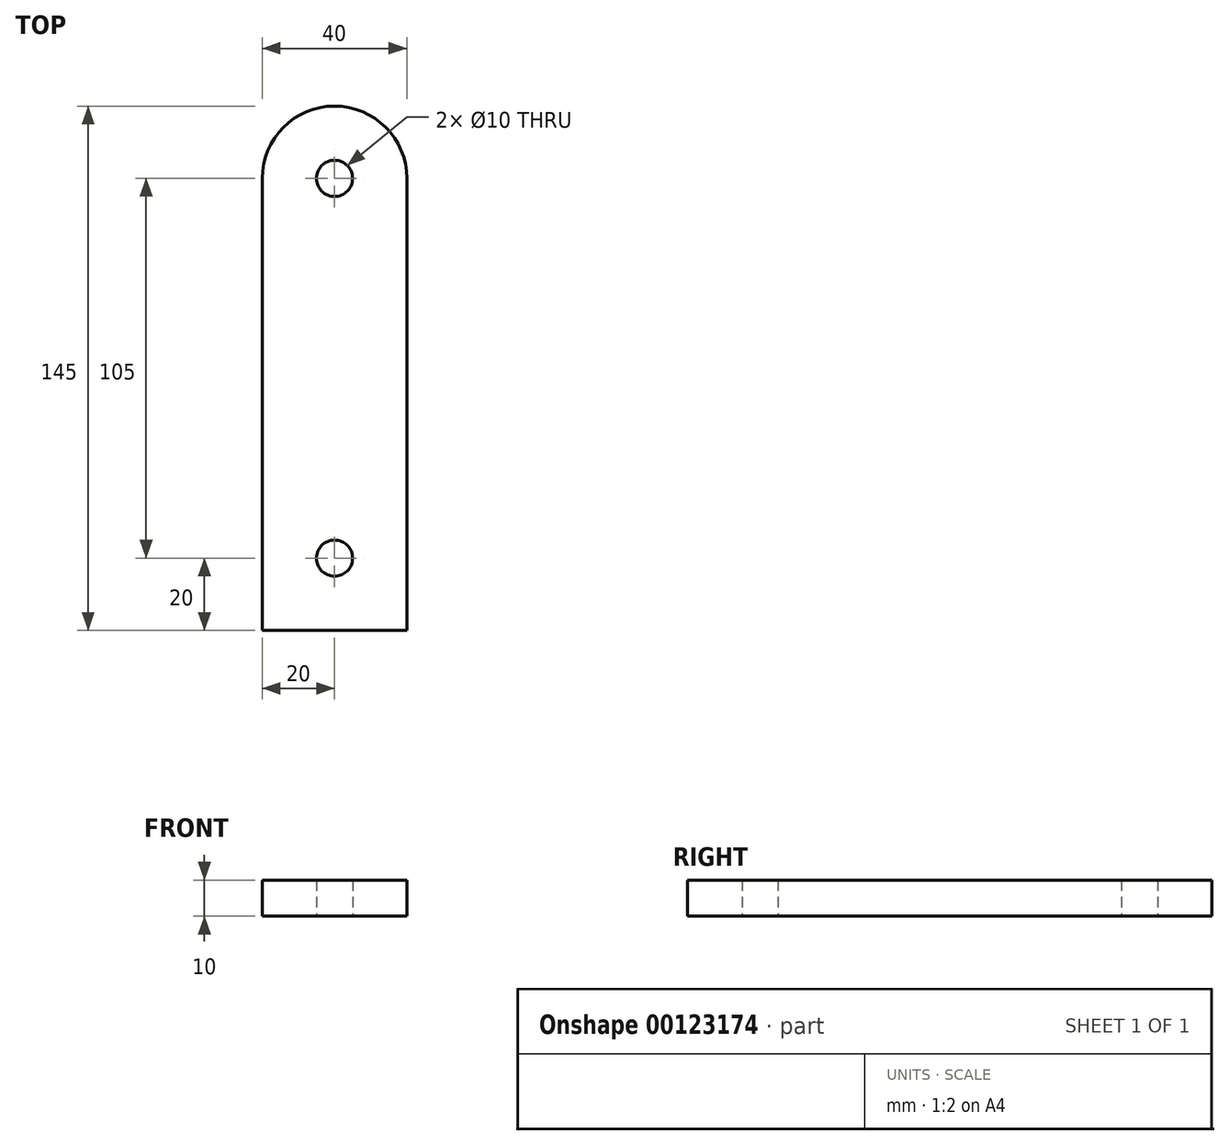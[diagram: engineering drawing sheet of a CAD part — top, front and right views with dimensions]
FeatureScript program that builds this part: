
annotation { "Feature Type Name" : "Feature", "Feature Type Description" : "" }
export const myFeature = defineFeature(function(context is Context, id is Id, definition is map)
    precondition{}
    {
        {
            var Q0;
            Q0=qCreatedBy(makeId("Top.planeOp"),FACE);
            var sketch = newSketch(context, id + "F0", { "sketchPlane" : qUnion([Q0])});
            skLineSegment(sketch, "E0.bottom", {"start": v(20, -62.5) * mm, "end": v(-20, -62.5) * mm});
            skLineSegment(sketch, "E0.top", {"start": v(20, 62.5) * mm, "end": v(-20, 62.5) * mm, "construction": true});
            skLineSegment(sketch, "E0.left", {"start": v(20, -62.5) * mm, "end": v(20, 62.5) * mm});
            skLineSegment(sketch, "E0.right", {"start": v(-20, -62.5) * mm, "end": v(-20, 62.5) * mm});
            skPoint(sketch, "E0.middle", {"position": v(0, 0) * mm});
            skArc(sketch, "E1", {"start": v(20, 62.5) * mm, "mid": v(0, 82.5) * mm, "end": v(-20, 62.5) * mm});
            skCircle(sketch, "E2", {"center": v(0, 62.5) * mm, "radius": 5 * mm});
            skCircle(sketch, "E3", {"center": v(0, -42.5) * mm, "radius": 5 * mm});
            skSolve(sketch);
        }
        {
            var Q0;
            Q0 = qSketchRegion(id + "F0", true);
            extrude(context, id + "F1", {"entities" : qUnion([Q0]), "depth" : 10 * mm});
        }
    });
